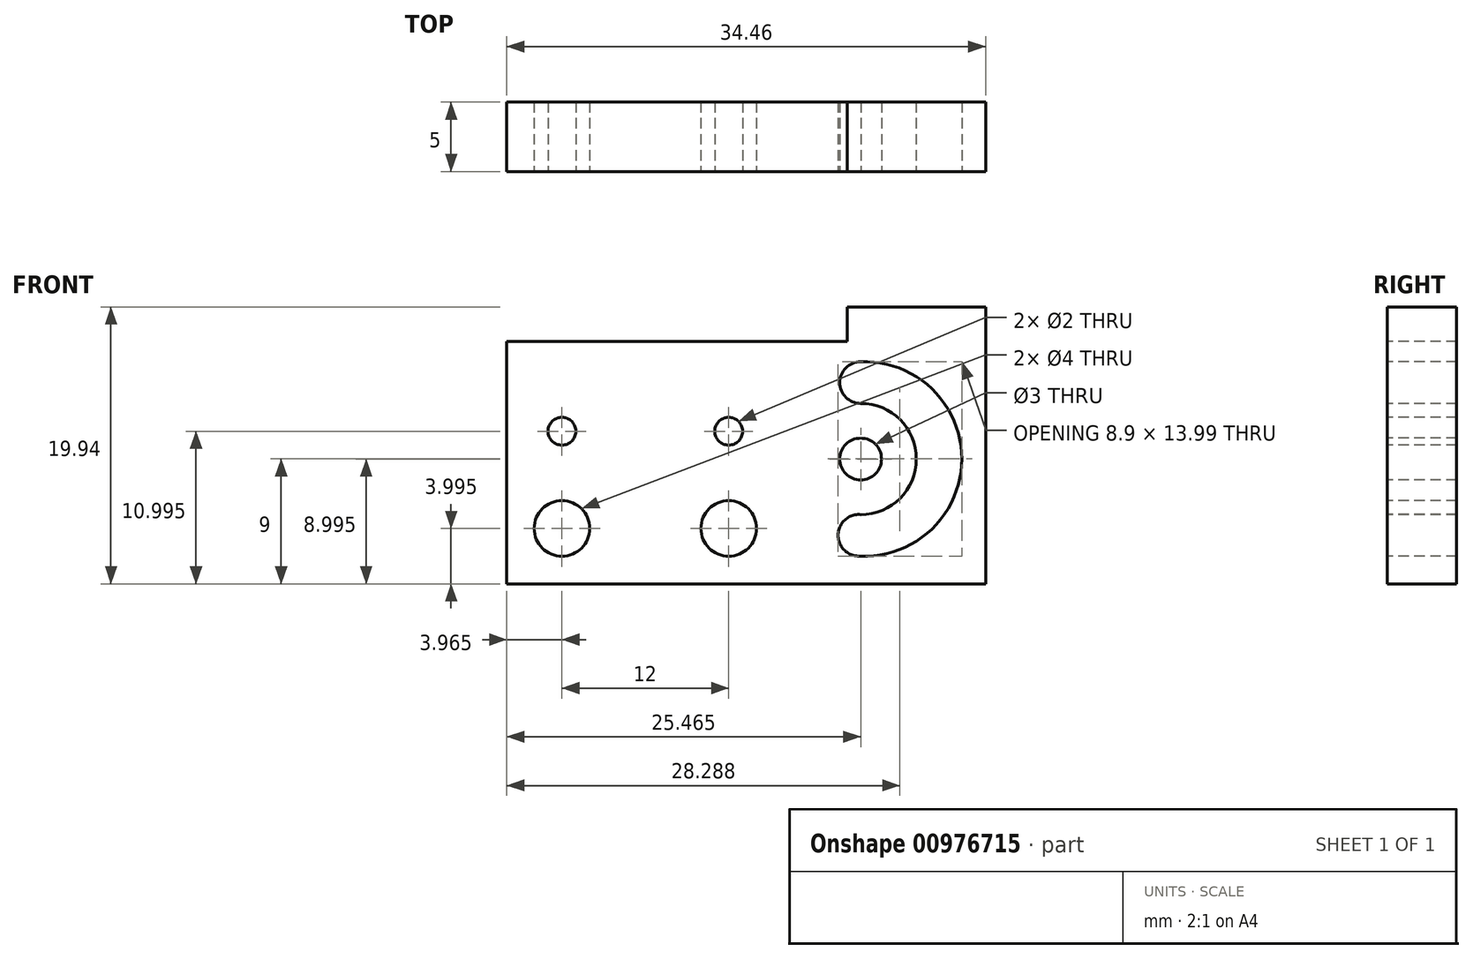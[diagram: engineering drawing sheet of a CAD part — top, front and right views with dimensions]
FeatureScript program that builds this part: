
annotation { "Feature Type Name" : "Feature", "Feature Type Description" : "" }
export const myFeature = defineFeature(function(context is Context, id is Id, definition is map)
    precondition{}
    {
        {
            var Q0;
            Q0=qCreatedBy(makeId("Front.planeOp"),FACE);
            var sketch = newSketch(context, id + "F0", { "sketchPlane" : qUnion([Q0])});
            skLineSegment(sketch, "E0.bottom", {"start": v(17.23, -9.97) * mm, "end": v(-17.23, -9.98) * mm});
            skLineSegment(sketch, "E0.top", {"start": v(17.23, 9.98) * mm, "end": v(-17.23, 9.97) * mm});
            skLineSegment(sketch, "E0.left", {"start": v(17.23, -9.97) * mm, "end": v(17.23, 9.98) * mm});
            skLineSegment(sketch, "E0.right", {"start": v(-17.23, -9.97) * mm, "end": v(-17.23, 9.97) * mm});
            skPoint(sketch, "E0.middle", {"position": v(0, 0) * mm});
            skSolve(sketch);
        }
        {
            var Q0;
            Q0 = qSketchRegion(id + "F0", true);
            extrude(context, id + "F1", {"entities" : qUnion([Q0]), "oppositeDirection" : true, "depth" : 5 * mm, "offsetDistance" : 25 * mm});
        }
        {
            var Q0;
            Q0=makeQuery(id+"F1.opExtrude","CAP_FACE",FACE,{"disambiguationData":[OSD([sQuery(id+"F0.wireOp",EDGE,"E0.bottom"),sQuery(id+"F0.wireOp",EDGE,"E0.top"),sQuery(id+"F0.wireOp",EDGE,"E0.left"),sQuery(id+"F0.wireOp",EDGE,"E0.right")])],"isStart":true});
            var sketch = newSketch(context, id + "F2", { "sketchPlane" : qUnion([Q0])});
            skLineSegment(sketch, "E1.bottom", {"start": v(-17.23, 9.97) * mm, "end": v(7.25, 9.97) * mm});
            skLineSegment(sketch, "E1.top", {"start": v(-17.23, 7.47) * mm, "end": v(7.25, 7.47) * mm});
            skLineSegment(sketch, "E1.left", {"start": v(-17.23, 9.97) * mm, "end": v(-17.23, 7.47) * mm});
            skLineSegment(sketch, "E1.right", {"start": v(7.25, 9.97) * mm, "end": v(7.25, 7.47) * mm});
            skSolve(sketch);
        }
        {
            var Q0;
            Q0 = qSketchRegion(id + "F2", true);
            extrude(context, id + "F3", {"entities" : qUnion([Q0]), "operationType" : NewBodyOperationType.REMOVE, "endBound" : BoundingType.UP_TO_NEXT, "oppositeDirection" : true, "depth" : 25 * mm, "offsetDistance" : 25 * mm});
        }
        {
            var Q0;
            Q0=makeQuery(id+"F1.opExtrude","CAP_FACE",FACE,{"disambiguationData":[OSD([sQuery(id+"F0.wireOp",EDGE,"E0.bottom"),sQuery(id+"F0.wireOp",EDGE,"E0.top"),sQuery(id+"F0.wireOp",EDGE,"E0.left"),sQuery(id+"F0.wireOp",EDGE,"E0.right")])],"isStart":true});
            var sketch = newSketch(context, id + "F4", { "sketchPlane" : qUnion([Q0])});
            skLineSegment(sketch, "E2", {"start": v(17.23, -9.97) * mm, "end": v(-1.26, -9.97) * mm});
            skLineSegment(sketch, "E3", {"start": v(-1.26, -9.97) * mm, "end": v(-1.26, -5.97) * mm});
            skLineSegment(sketch, "E4", {"start": v(-1.26, -5.97) * mm, "end": v(-13.26, -5.97) * mm});
            skLineSegment(sketch, "E5", {"start": v(-1.26, -9.97) * mm, "end": v(-1.26, 1.03) * mm});
            skLineSegment(sketch, "E6", {"start": v(-13.26, -5.97) * mm, "end": v(-13.26, 1.03) * mm});
            skCircle(sketch, "E7", {"center": v(-13.26, -5.97) * mm, "radius": 2 * mm});
            skCircle(sketch, "E8", {"center": v(-1.26, -5.97) * mm, "radius": 2 * mm});
            skCircle(sketch, "E9", {"center": v(-13.26, 1.03) * mm, "radius": 1 * mm});
            skCircle(sketch, "E10", {"center": v(-1.26, 1.03) * mm, "radius": 1 * mm});
            skSolve(sketch);
        }
        {
            var Q0;
            Q0 = qSketchRegion(id + "F4", true);
            extrude(context, id + "F5", {"entities" : qUnion([Q0]), "operationType" : NewBodyOperationType.REMOVE, "endBound" : BoundingType.UP_TO_NEXT, "oppositeDirection" : true, "depth" : 25 * mm, "offsetDistance" : 25 * mm});
        }
        {
            var Q0;
            Q0=makeQuery(id+"F1.opExtrude","CAP_FACE",FACE,{"disambiguationData":[OSD([sQuery(id+"F0.wireOp",EDGE,"E0.bottom"),sQuery(id+"F0.wireOp",EDGE,"E0.top"),sQuery(id+"F0.wireOp",EDGE,"E0.left"),sQuery(id+"F0.wireOp",EDGE,"E0.right")])],"isStart":true});
            var sketch = newSketch(context, id + "F6", { "sketchPlane" : qUnion([Q0])});
            skLineSegment(sketch, "E11", {"start": v(17.23, -9.97) * mm, "end": v(8.23, -9.97) * mm});
            skLineSegment(sketch, "E12", {"start": v(8.23, -9.97) * mm, "end": v(8.23, -0.97) * mm});
            skCircle(sketch, "E13", {"center": v(8.23, -0.97) * mm, "radius": 1.5 * mm});
            skLineSegment(sketch, "E14", {"start": v(12.23, -0.97) * mm, "end": v(10.73, -0.97) * mm});
            skArc(sketch, "E15", {"start": v(8.23, -4.97) * mm, "mid": v(12.23, -0.97) * mm, "end": v(8.23, 3.03) * mm});
            skArc(sketch, "E16", {"start": v(8.23, -7.96) * mm, "mid": v(15.5, -0.97) * mm, "end": v(8.23, 6.03) * mm});
            skArc(sketch, "E17", {"start": v(8.23, -4.97) * mm, "mid": v(6.6, -6.47) * mm, "end": v(8.23, -7.96) * mm});
            skArc(sketch, "E18", {"start": v(8.23, 6.03) * mm, "mid": v(6.73, 4.53) * mm, "end": v(8.23, 3.03) * mm});
            skSolve(sketch);
        }
        {
            var Q0;
            Q0 = qSketchRegion(id + "F6", true);
            extrude(context, id + "F7", {"entities" : qUnion([Q0]), "operationType" : NewBodyOperationType.REMOVE, "endBound" : BoundingType.UP_TO_NEXT, "oppositeDirection" : true, "depth" : 25 * mm, "offsetDistance" : 25 * mm});
        }
    });
